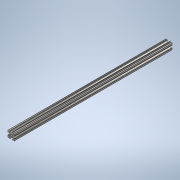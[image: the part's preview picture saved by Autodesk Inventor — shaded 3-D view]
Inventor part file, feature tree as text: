
AUTODESK INVENTOR PART (.ipt)
format: ipt  version: 2020 (Build 240168000, 168)  size: 242,176 bytes
history: native  units: in
note: dims shown in document units (in); Inventor stores cm internally (conversion verified against a paired STEP export)
features: extrude x1, sketch x1
ambient origin geometry x8: Origin, YZ Plane, XZ Plane, XY Plane, X Axis, Y Axis, Z Axis, Center Point
bodies: Solid1 (feature_tree)
feature tree (2):
  extrude  "Extrusion1"  [1 undecoded]
  sketch  "Sketch1"  dims[d0=23.0in d1=0.0in]
note: 1 required parameter value undecoded (feature->parameter linkage not recoverable at this tier; creation-order binding heuristic only, values carry confidence <= 0.55)
